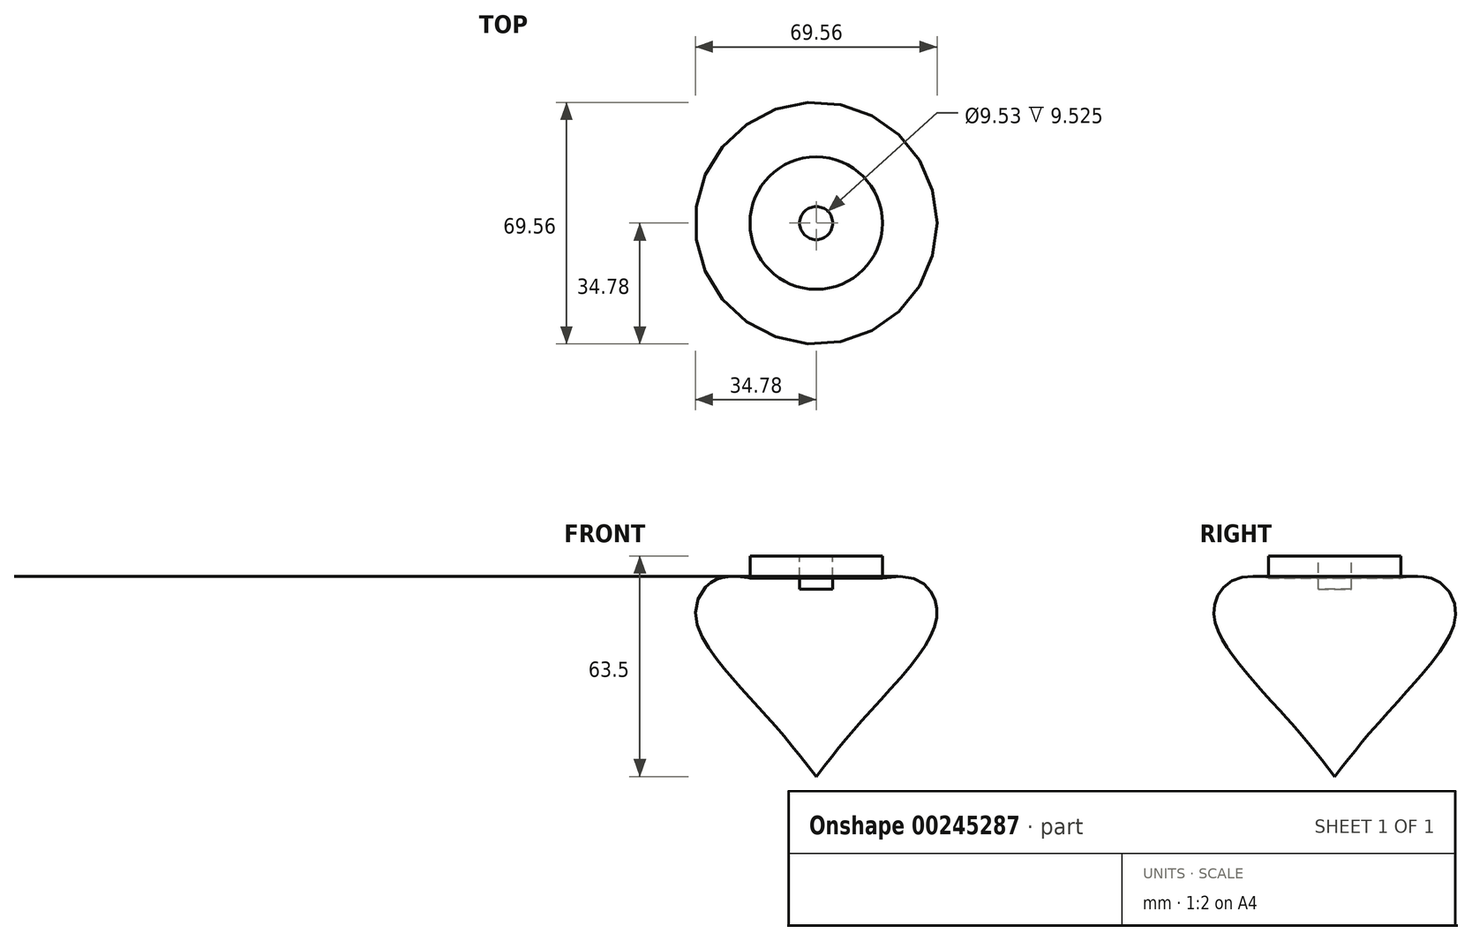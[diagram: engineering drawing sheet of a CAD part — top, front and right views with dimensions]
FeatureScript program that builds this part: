
annotation { "Feature Type Name" : "Feature", "Feature Type Description" : "" }
export const myFeature = defineFeature(function(context is Context, id is Id, definition is map)
    precondition{}
    {
        {
            var Q0;
            Q0=qCreatedBy(makeId("Front.planeOp"),FACE);
            var sketch = newSketch(context, id + "F0", { "sketchPlane" : qUnion([Q0])});
            skLineSegment(sketch, "E0", {"start": v(0, 63.5) * mm, "end": v(0, 0) * mm});
            skLineSegment(sketch, "E1", {"start": v(0, 63.5) * mm, "end": v(19.05, 63.5) * mm});
            skLineSegment(sketch, "E2", {"start": v(19.05, 63.5) * mm, "end": v(19.05, 57.15) * mm});
            skFitSpline(sketch, "E3", {"points": [v(0, 0) * mm, v(13, 15.88) * mm, v(31.16, 37.36) * mm, v(34.48, 49.76) * mm, v(19.05, 57.15) * mm], "startDerivative": vector(56.25, 72.08) * mm, "endDerivative": vector(-131.3, -25.36) * mm});
            skSolve(sketch);
        }
        {
            var Q0;
            Q0=makeQuery(id+"F0.imprint","IMPRINT",FACE,{"disambiguationData":[TD([[makeQuery(id+"F0.imprint","IMPRINT",EDGE,{"derivedFrom":sQuery(id+"F0.wireOp",EDGE,"E0")}),1.0]])]});
            var Q1;
            Q1=sQuery(id+"F0.wireOp",EDGE,"E0");
            revolve(context, id + "F1", {"entities" : qUnion([Q0]), "axis" : qUnion([Q1]), "revolveType" : RevolveType.FULL});
        }
        {
            var Q0;
            Q0=makeQuery(id+"F1.opRevolve","SWEPT_FACE",FACE,{"disambiguationData":[OSD([sQuery(id+"F0.wireOp",EDGE,"E1")])]});
            var sketch = newSketch(context, id + "F2", { "sketchPlane" : qUnion([Q0])});
            skCircle(sketch, "E4", {"center": v(0, 0) * mm, "radius": 4.76 * mm});
            skSolve(sketch);
        }
        {
            var Q0;
            Q0=makeQuery(id+"F2.imprint","IMPRINT",FACE,{"disambiguationData":[TD([[makeQuery(id+"F2.imprint","IMPRINT",EDGE,{"derivedFrom":sQuery(id+"F2.wireOp",EDGE,"E4")}),1.0]])]});
            extrude(context, id + "F3", {"entities" : qUnion([Q0]), "operationType" : NewBodyOperationType.REMOVE, "oppositeDirection" : true, "depth" : 9.52 * mm});
        }
        {
            var Q0;
            Q0=qCreatedBy(makeId("Top.planeOp"),FACE);
            var sketch = newSketch(context, id + "F4", { "sketchPlane" : qUnion([Q0])});
            skCircle(sketch, "E5", {"center": v(0, 0) * mm, "radius": 1.59 * mm});
            skSolve(sketch);
        }
        {
            var Q0;
            Q0=sQuery(id+"F4.wireOp",EDGE,"E5");
            extrude(context, id + "F5", {"bodyType" : ToolBodyType.SURFACE, "operationType" : NewBodyOperationType.REMOVE, "surfaceEntities" : qUnion([Q0]), "depth" : 22.22 * mm});
        }
    });
